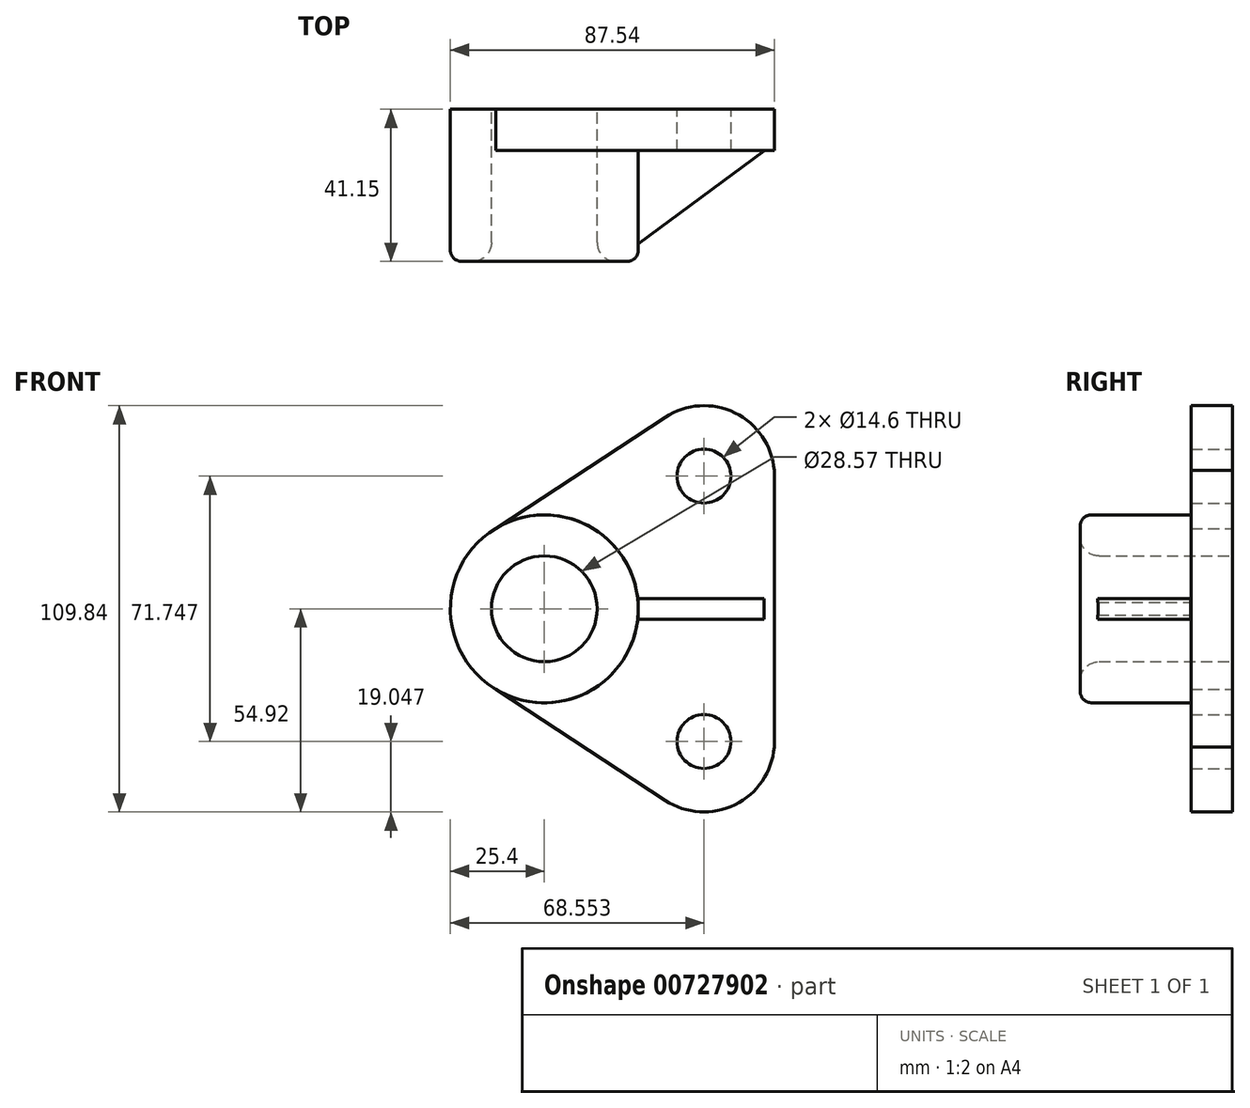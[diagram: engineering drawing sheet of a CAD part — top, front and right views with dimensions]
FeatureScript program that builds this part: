
annotation { "Feature Type Name" : "Feature", "Feature Type Description" : "" }
export const myFeature = defineFeature(function(context is Context, id is Id, definition is map)
    precondition{}
    {
        {
            var Q0;
            Q0=qCreatedBy(makeId("Front.planeOp"),FACE);
            var sketch = newSketch(context, id + "F0", { "sketchPlane" : qUnion([Q0])});
            skCircle(sketch, "E0", {"center": v(0, 0) * mm, "radius": 14.29 * mm});
            skCircle(sketch, "E1", {"center": v(0, 0) * mm, "radius": 25.4 * mm});
            skLineSegment(sketch, "E2", {"start": v(-13.16, 21.72) * mm, "end": v(32.7, 51.8) * mm});
            skLineSegment(sketch, "E3", {"start": v(-13.16, -21.72) * mm, "end": v(32.7, -51.8) * mm});
            skArc(sketch, "E4", {"start": v(62.14, 37.39) * mm, "mid": v(51.53, 52.98) * mm, "end": v(32.7, 51.8) * mm});
            skLineSegment(sketch, "E5", {"start": v(62.14, 37.39) * mm, "end": v(62.14, -37.39) * mm});
            skArc(sketch, "E6", {"start": v(32.7, -51.8) * mm, "mid": v(51.53, -52.98) * mm, "end": v(62.14, -37.39) * mm});
            skCircle(sketch, "E7", {"center": v(43.15, 35.87) * mm, "radius": 7.3 * mm});
            skCircle(sketch, "E8", {"center": v(43.15, -35.87) * mm, "radius": 7.3 * mm});
            skSolve(sketch);
        }
        {
            var Q0;
            Q0=makeQuery(id+"F0.imprint","IMPRINT",FACE,{"disambiguationData":[TD([[makeQuery(id+"F0.imprint","IMPRINT",EDGE,{"derivedFrom":sQuery(id+"F0.wireOp",EDGE,"E0")}),-1.0]])]});
            extrude(context, id + "F1", {"entities" : qUnion([Q0]), "depth" : 41.15 * mm, "offsetDistance" : 25.4 * mm});
        }
        {
            var Q0;
            {var subQ1=sQuery(id+"F0.wireOp",EDGE,"E2");Q0=makeQuery(id+"F0.imprint","IMPRINT",FACE,{"disambiguationData":[TD([[makeQuery(id+"F0.imprint","IMPRINT",EDGE,{"derivedFrom":subQ1}),-1.0]])]});}
            extrude(context, id + "F2", {"entities" : qUnion([Q0]), "operationType" : NewBodyOperationType.ADD, "depth" : 11.18 * mm, "offsetDistance" : 25.4 * mm});
        }
        {
            var Q0;
            Q0=makeQuery(id+"F1.opExtrude","CAP_EDGE",EDGE,{"disambiguationData":[OSD([sQuery(id+"F0.wireOp",EDGE,"E0")])],"isStart":false});
            fillet(context, id + "F3", {"entities" : qUnion([Q0]), "radius" : 5.08 * mm, "tangentPropagation" : true, "allowEdgeOverflow" : false});
        }
        {
            var Q0;
            Q0=makeQuery(id+"F1.opExtrude","CAP_EDGE",EDGE,{"disambiguationData":[OSD([sQuery(id+"F0.wireOp",EDGE,"E1")])],"isStart":false});
            fillet(context, id + "F4", {"entities" : qUnion([Q0]), "radius" : 3.05 * mm, "tangentPropagation" : true, "allowEdgeOverflow" : false});
        }
        {
            var Q0;
            Q0=qCreatedBy(makeId("Top.planeOp"),FACE);
            var sketch = newSketch(context, id + "F5", { "sketchPlane" : qUnion([Q0])});
            skLineSegment(sketch, "E9", {"start": v(25.34, -11.2) * mm, "end": v(25.34, -36.38) * mm});
            skLineSegment(sketch, "E10", {"start": v(25.34, -36.38) * mm, "end": v(59.4, -11.27) * mm});
            skLineSegment(sketch, "E11", {"start": v(59.4, -11.27) * mm, "end": v(25.34, -11.2) * mm});
            skSolve(sketch);
        }
        {
            var Q0;
            Q0=makeQuery(id+"F5.imprint","IMPRINT",FACE,{"disambiguationData":[TD([[makeQuery(id+"F5.imprint","IMPRINT",EDGE,{"derivedFrom":sQuery(id+"F5.wireOp",EDGE,"E9")}),1.0]])]});
            extrude(context, id + "F6", {"entities" : qUnion([Q0]), "operationType" : NewBodyOperationType.ADD, "endBound" : BoundingType.SYMMETRIC, "depth" : 5.6 * mm, "offsetDistance" : 25.4 * mm});
        }
    });
